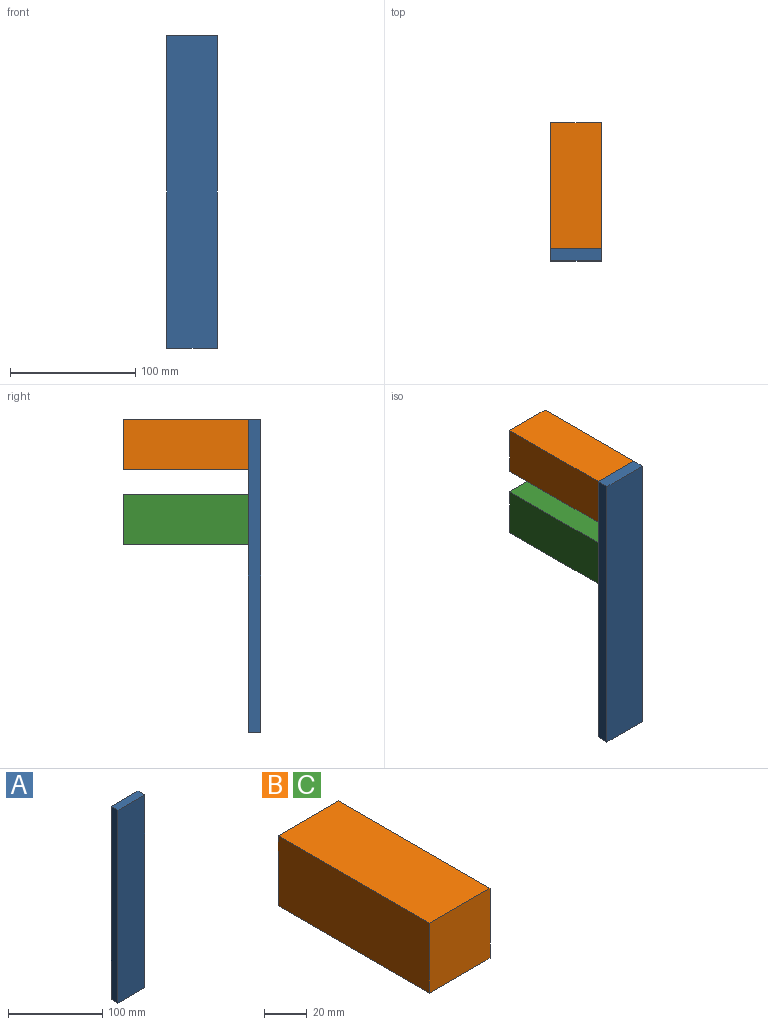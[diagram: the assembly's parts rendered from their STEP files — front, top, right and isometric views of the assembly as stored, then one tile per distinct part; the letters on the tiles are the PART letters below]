
ASSEMBLY  parts=3 mates=1
PART A: 6 faces, bbox 40x10x250 mm
  f0: plane 40x10mm, normal (0,0,1), area 400mm2, adj f1,f3,f4,f5
  f1: plane 250x10mm, normal (-1,0,0), area 2500mm2, adj f0,f2,f4,f5
  f2: plane 40x10mm, normal (0,0,-1), area 400mm2, adj f1,f3,f4,f5
  f3: plane 250x10mm, normal (1,0,0), area 2500mm2, adj f0,f2,f4,f5
  f4: plane 250x40mm, normal (0,1,0), area 10000mm2, adj f0,f1,f2,f3
  f5: plane 250x40mm, normal (0,-1,0), area 10000mm2, adj f0,f1,f2,f3
PART B: 6 faces, bbox 40x100x40 mm
  f0: plane 100x40mm, normal (0,0,1), area 4000mm2, adj f1,f3,f4,f5
  f1: plane 100x40mm, normal (-1,0,0), area 4000mm2, adj f0,f2,f4,f5
  f2: plane 100x40mm, normal (0,0,-1), area 4000mm2, adj f1,f3,f4,f5
  f3: plane 100x40mm, normal (1,0,0), area 4000mm2, adj f0,f2,f4,f5
  f4: plane 40x40mm, normal (0,1,0), area 1600mm2, adj f0,f1,f2,f3
  f5: plane 40x40mm, normal (0,-1,0), area 1600mm2, adj f0,f1,f2,f3
PART C: same geometry as B
PLACE A t=(12.1,-10,-51.28)mm
PLACE B t=(0,0,-40)mm
PLACE C t=(0,0,-100)mm
MATE fastened B.f5 <-> A.f4  axis (0,-1,0) through (0,0,0)mm
